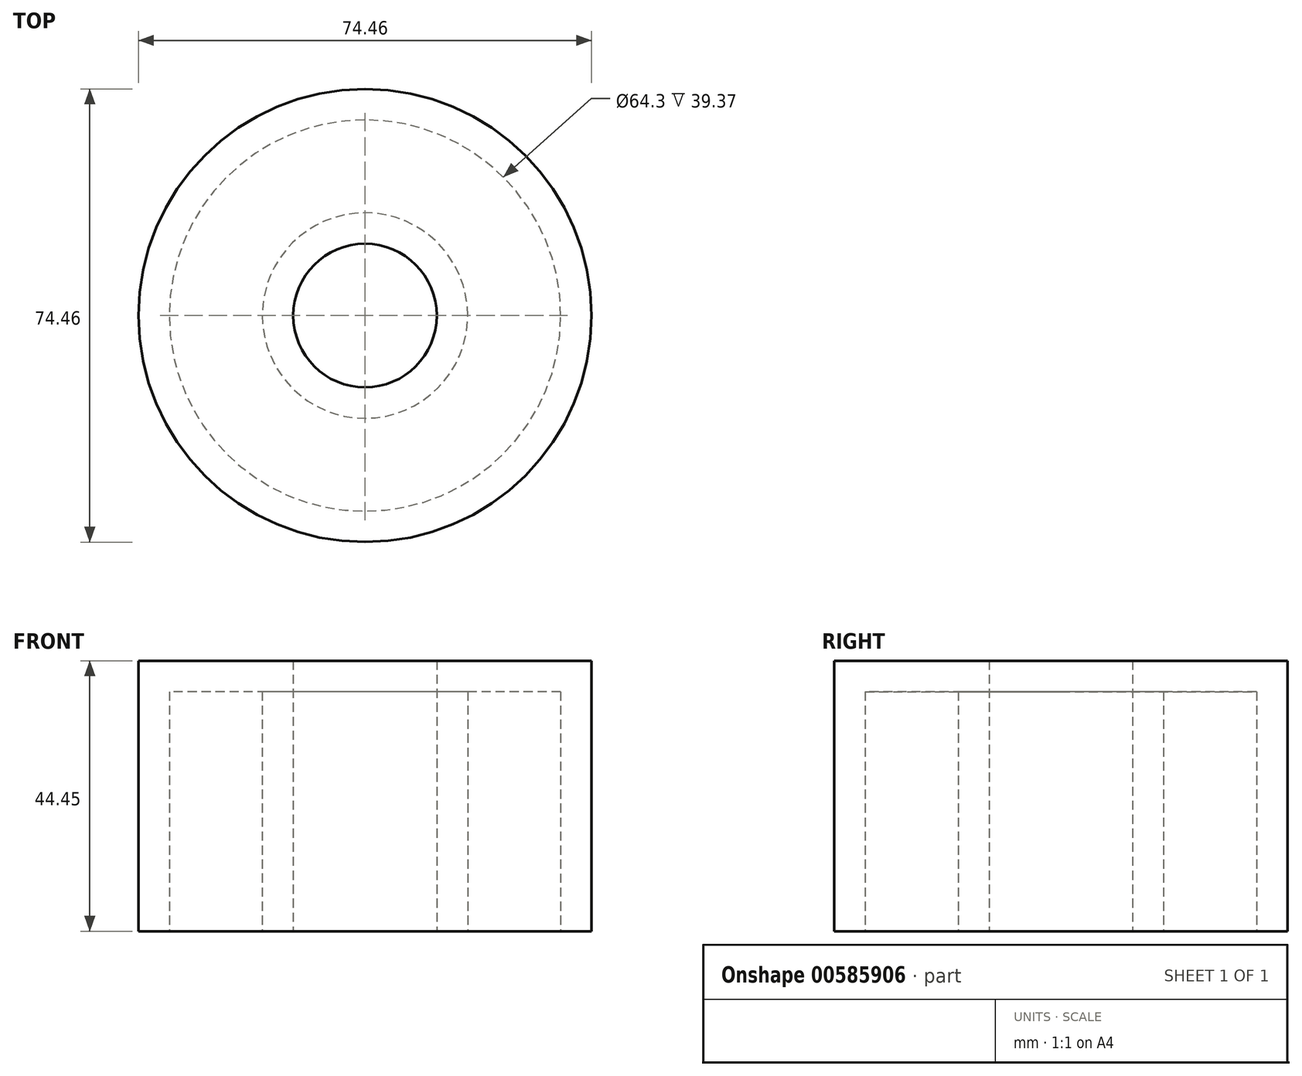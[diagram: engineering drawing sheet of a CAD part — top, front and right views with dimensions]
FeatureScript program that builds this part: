
annotation { "Feature Type Name" : "Feature", "Feature Type Description" : "" }
export const myFeature = defineFeature(function(context is Context, id is Id, definition is map)
    precondition{}
    {
        {
            var Q0;
            Q0=qCreatedBy(makeId("Top.planeOp"),FACE);
            var sketch = newSketch(context, id + "F0", { "sketchPlane" : qUnion([Q0])});
            skCircle(sketch, "E0", {"center": v(0, 0) * mm, "radius": 37.23 * mm});
            skCircle(sketch, "E1", {"center": v(0, 0) * mm, "radius": 11.8 * mm});
            skSolve(sketch);
        }
        {
            var Q0;
            Q0 = qSketchRegion(id + "F0", true);
            extrude(context, id + "F1", {"entities" : qUnion([Q0]), "depth" : 44.45 * mm, "offsetDistance" : 25.4 * mm});
        }
        {
            var Q0;
            Q0=makeQuery(id+"F1.opExtrude","CAP_FACE",FACE,{"disambiguationData":[OSD([sQuery(id+"F0.wireOp",EDGE,"E0"),sQuery(id+"F0.wireOp",EDGE,"E1")])],"isStart":true});
            shell(context, id + "F2", {"entities" : qUnion([Q0]), "thickness" : 5.08 * mm});
        }
    });
